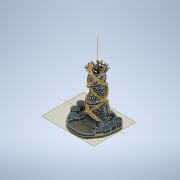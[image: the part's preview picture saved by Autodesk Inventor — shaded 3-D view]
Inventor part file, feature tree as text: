
AUTODESK INVENTOR PART (.ipt)
format: ipt  version: 2022 (Build 260153000, 153)  size: 9,097,728 bytes
history: native  units: mm
features: sketch x24, extrude x17, helix x5, plane x3, fillet x3, revolve x2, pattern_circular x2
ambient origin geometry x8: Origin, YZ Plane, XZ Plane, XY Plane, X Axis, Y Axis, Z Axis, Center Point
bodies: Solid1 (feature_tree)
feature tree (56):
  revolve  "Revolution1"  [1 undecoded]
  plane  "Work Plane1"
  extrude  "Extrusion4"  Depth=20.0mm
  extrude  "Extrusion2"  Depth=29.0mm
  pattern_circular  "Circular Pattern2"  Count=12  [1 undecoded]
  plane  "Work Plane3"
  extrude  "Extrusion3"  Depth=10.0mm
  pattern_circular  "Circular Pattern3"  Count=7  [1 undecoded]
  helix  "Coil1"  [1 undecoded]
  helix  "Coil2"  [1 undecoded]
  helix  "Coil3"  [1 undecoded]
  helix  "Coil4"  [1 undecoded]
  helix  "Coil5"  [1 undecoded]
  extrude  "Extrusion5"  Depth=20.0mm
  revolve  "Revolution2"  [1 undecoded]
  extrude  "Extrusion6"  Depth=30.0mm
  extrude  "Extrusion7"  Depth=15.0mm
  fillet  "Fillet1"  Radius=15.0mm
  fillet  "Fillet2"  Radius=30.0mm
  extrude  "Extrusion15"  Depth=45.0mm
  extrude  "Extrusion16"  Depth=13.0mm
  extrude  "Extrusion17"  Depth=39.0mm
  extrude  "Extrusion18"  Depth=11.0mm
  extrude  "Extrusion19"  Depth=10.0mm
  extrude  "Extrusion20"  Depth=11.0mm
  extrude  "Extrusion21"  Depth=9.0mm
  extrude  "Extrusion22"  Depth=3.0mm TaperAngle=0.0deg
  extrude  "Extrusion23"  Depth=60.0mm
  extrude  "Extrusion25"  Depth=46.0mm
  fillet  "Fillet3"  [1 undecoded]
  extrude  "Extrusion26"  Depth=70.0mm
  sketch  "Sketch1"  dims[d11=60.0mm d12=40.0mm]
  sketch  "Sketch3"  dims[d13=20.0mm d14=20.0mm]
  plane  "Work Plane2"
  sketch  "Sketch4"  dims[d15=20.0mm d16=29.0mm d17=120.0mm]
  sketch  "Sketch5"  dims[d18=50.0mm d19=10.0mm]
  sketch  "Sketch7"  dims[d20=209.0mm]
  sketch  "Sketch8"  dims[d26=2.0mm]
  sketch  "Sketch9"  dims[d27=2.0mm]
  sketch  "Sketch10"  dims[d28=2.0mm]
  sketch  "Sketch11"  dims[d29=2.0mm]
  sketch  "Sketch13"  dims[d30=2.0mm]
  sketch  "Sketch16"  dims[d31=90.0deg d32=70.0mm d38=77.75mm d39=0.0mm d40=40.0mm d41=360.0deg d43=70.0mm d44=77.75mm d45=0.0mm d46=40.0mm d47=360.0deg]
  sketch  "Sketch17"  dims[d49=20.0mm d50=20.0mm]
  sketch  "Sketch19"  dims[d51=20.0mm d52=20.0mm]
  sketch  "Sketch20"  dims[d53=40.0mm d54=30.0mm]
  sketch  "Sketch21"  dims[d55=30.0mm d56=15.0mm d57=15.0mm d58=30.0mm]
  sketch  "Sketch22"  dims[d59=77.75mm d60=0.0mm d61=45.0mm]
  sketch  "Sketch23"  dims[d62=35.0mm]
  sketch  "Sketch24"  dims[d63=70.0mm d64=150.0mm d65=10.0mm d66=-0.567232mm d67=90.0deg d68=90.0deg d69=90.0deg d70=90.0deg d71=13.0mm]
  sketch  "Sketch25"  dims[d72=10.0mm d73=39.0mm]
  sketch  "Sketch26"  dims[d74=150.0mm d75=210.0mm d76=10.0mm d77=-0.645772mm d78=90.0deg d79=90.0deg d80=90.0deg d81=90.0deg d82=11.0mm]
  sketch  "Sketch27"  dims[d83=39.0mm d84=10.0mm]
  sketch  "Sketch28"  dims[d85=170.0mm d86=210.0mm d87=10.0mm d88=-0.645772mm d89=90.0deg d90=90.0deg d91=90.0deg d92=90.0deg d93=11.0mm]
  sketch  "Sketch30"  dims[d94=200.0mm d95=210.0mm d96=10.0mm d97=-0.645772mm d98=90.0deg d99=90.0deg d100=90.0deg d101=90.0deg d102=9.0mm]
  sketch  "Sketch31"  dims[d103=170.0mm d104=210.0mm d105=10.0mm d106=-0.645772mm d107=90.0deg d108=90.0deg d109=90.0deg d110=90.0deg d125=3.0mm d126=0.0mm d128=60.0mm d129=46.0mm d130=270.0deg d131=70.0mm d132=35.0mm d133=54.0mm d134=0.0mm d136=54.0mm d137=0.0mm d138=73.12351mm d139=5.0mm d140=5.0mm d141=30.0mm d165=30.0mm d166=25.0mm d167=25.0mm d168=25.0mm d169=25.0mm d170=30.0mm d171=30.0mm d172=30.0mm d173=65.0mm d174=40.0mm d177=65.0mm d180=130.0mm d181=110.0mm d182=60.0mm d183=90.0mm d184=110.0mm d186=5.0mm d187=10.0mm d188=0.0mm d190=5.0mm d191=0.0mm d192=10.0mm d193=0.0mm d194=15.0mm d195=0.0mm d196=0.2mm d197=0.0mm d198=5.0mm d199=0.0mm d200=10.0mm d201=0.0mm d202=15.0mm d203=0.0mm d204=10.0mm d205=0.0mm d210=7.0mm d211=0.0mm d212=3.6mm d213=10.0mm d214=0.0mm d135=0.0mm]
note: 10 required parameter values undecoded (feature->parameter linkage not recoverable at this tier; creation-order binding heuristic only, values carry confidence <= 0.55)